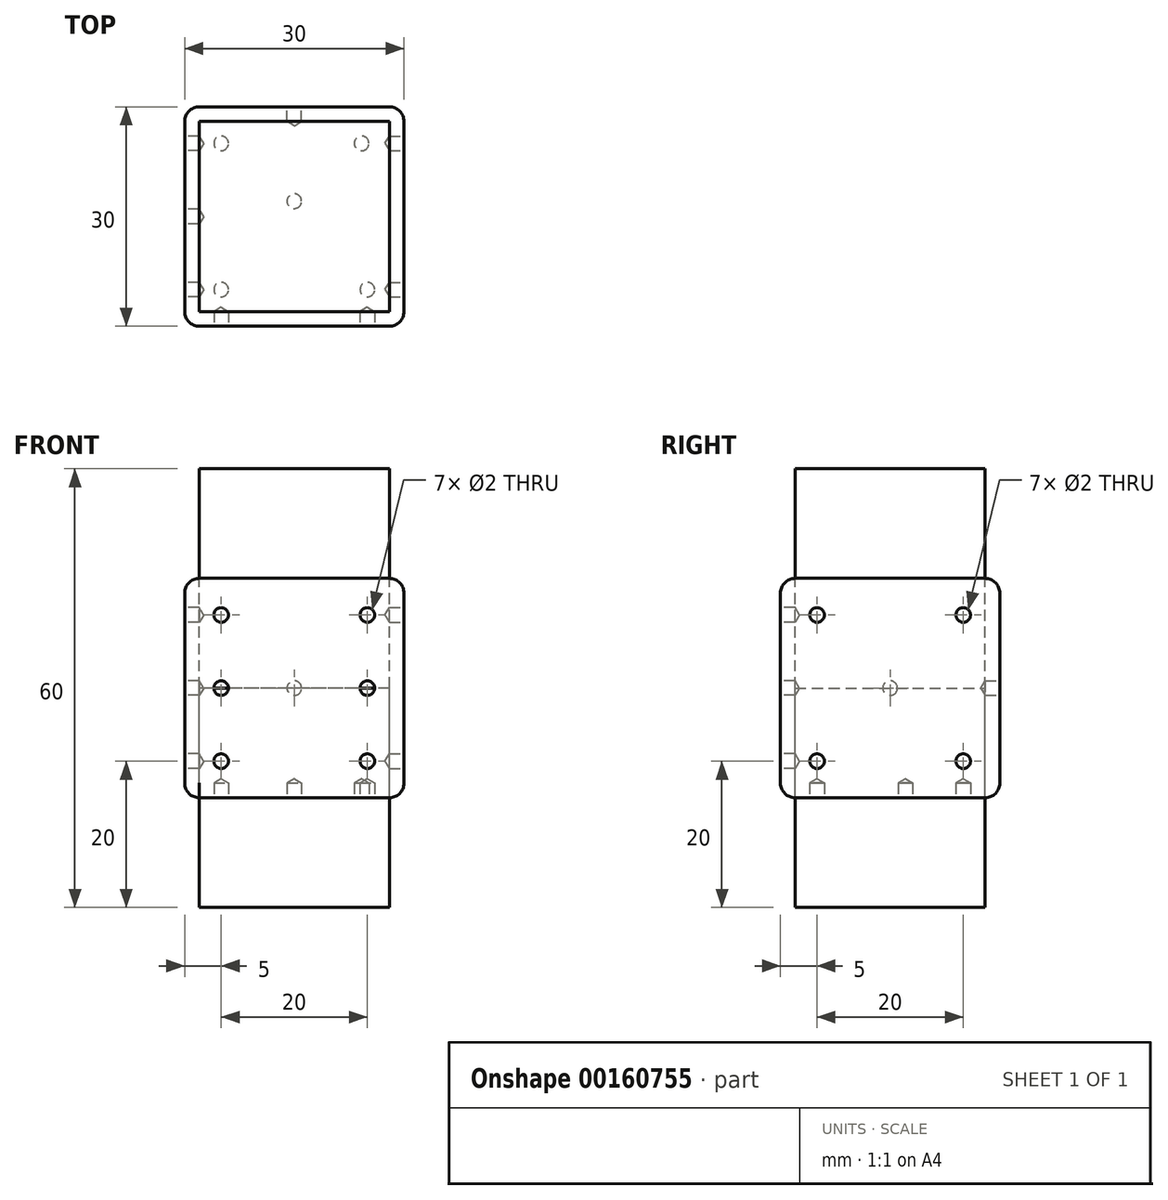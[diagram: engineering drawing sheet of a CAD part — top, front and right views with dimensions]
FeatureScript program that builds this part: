
annotation { "Feature Type Name" : "Feature", "Feature Type Description" : "" }
export const myFeature = defineFeature(function(context is Context, id is Id, definition is map)
    precondition{}
    {
        {
            var Q0;
            Q0=qCreatedBy(makeId("Front.planeOp"),FACE);
            var sketch = newSketch(context, id + "F0", { "sketchPlane" : qUnion([Q0])});
            skLineSegment(sketch, "E0.bottom", {"start": v(15, 15) * mm, "end": v(-15, 15) * mm});
            skLineSegment(sketch, "E0.top", {"start": v(15, -15) * mm, "end": v(-15, -15) * mm});
            skLineSegment(sketch, "E0.left", {"start": v(15, 15) * mm, "end": v(15, -15) * mm});
            skLineSegment(sketch, "E0.right", {"start": v(-15, 15) * mm, "end": v(-15, -15) * mm});
            skPoint(sketch, "E0.middle", {"position": v(0, 0) * mm});
            skLineSegment(sketch, "E1", {"start": v(15, 0) * mm, "end": v(-15, 0) * mm});
            skLineSegment(sketch, "E2", {"start": v(0, 0) * mm, "end": v(0, -15) * mm});
            skLineSegment(sketch, "E3", {"start": v(0, 0) * mm, "end": v(-15, 0) * mm});
            skLineSegment(sketch, "E4", {"start": v(0, 0) * mm, "end": v(0, 15) * mm});
            skPoint(sketch, "E5.middle", {"position": v(-15, 15) * mm});
            skPoint(sketch, "E6.middle", {"position": v(-15, -15) * mm});
            skPoint(sketch, "E7.middle", {"position": v(15, 15) * mm});
            skPoint(sketch, "E8.middle", {"position": v(15, -15) * mm});
            skSolve(sketch);
        }
        {
            var Q0;
            Q0 = qSketchRegion(id + "F0", true);
            extrude(context, id + "F1", {"entities" : qUnion([Q0]), "endBound" : BoundingType.SYMMETRIC, "depth" : 30 * mm});
        }
        {
            var Q0;
            Q0=makeQuery(id+"F1.opExtrude","CAP_EDGE",EDGE,{"disambiguationData":[OSD([sQuery(id+"F0.wireOp",EDGE,"E0.right")])],"isStart":false});
            var Q1;
            Q1=makeQuery(id+"F1.opExtrude","CAP_EDGE",EDGE,{"disambiguationData":[OSD([sQuery(id+"F0.wireOp",EDGE,"E0.top")])],"isStart":false});
            var Q2;
            Q2=makeQuery(id+"F1.opExtrude","SWEPT_EDGE",EDGE,{"disambiguationData":[OSD([sQuery(id+"F0.wireOp",EDGE,"E0.top"),sQuery(id+"F0.wireOp",EDGE,"E0.right")])]});
            var Q3;
            Q3=makeQuery(id+"F1.opExtrude","CAP_EDGE",EDGE,{"disambiguationData":[OSD([sQuery(id+"F0.wireOp",EDGE,"E0.top")])],"isStart":true});
            var Q4;
            Q4=makeQuery(id+"F1.opExtrude","CAP_EDGE",EDGE,{"disambiguationData":[OSD([sQuery(id+"F0.wireOp",EDGE,"E0.right")])],"isStart":true});
            var Q5;
            Q5=makeQuery(id+"F1.opExtrude","SWEPT_EDGE",EDGE,{"disambiguationData":[OSD([sQuery(id+"F0.wireOp",EDGE,"E0.bottom"),sQuery(id+"F0.wireOp",EDGE,"E0.right")])]});
            var Q6;
            Q6=makeQuery(id+"F1.opExtrude","CAP_EDGE",EDGE,{"disambiguationData":[OSD([sQuery(id+"F0.wireOp",EDGE,"E0.bottom")])],"isStart":false});
            var Q7;
            Q7=makeQuery(id+"F1.opExtrude","CAP_FACE",FACE,{"disambiguationData":[OSD([sQuery(id+"F0.wireOp",EDGE,"E0.bottom"),sQuery(id+"F0.wireOp",EDGE,"E0.top"),sQuery(id+"F0.wireOp",EDGE,"E0.left"),sQuery(id+"F0.wireOp",EDGE,"E0.right")])],"isStart":false});
            var Q8;
            Q8=makeQuery(id+"F1.opExtrude","SWEPT_EDGE",EDGE,{"disambiguationData":[OSD([sQuery(id+"F0.wireOp",EDGE,"E0.bottom"),sQuery(id+"F0.wireOp",EDGE,"E0.left")])]});
            var Q9;
            Q9=makeQuery(id+"F1.opExtrude","CAP_EDGE",EDGE,{"disambiguationData":[OSD([sQuery(id+"F0.wireOp",EDGE,"E0.bottom")])],"isStart":true});
            var Q10;
            Q10=makeQuery(id+"F1.opExtrude","CAP_EDGE",EDGE,{"disambiguationData":[OSD([sQuery(id+"F0.wireOp",EDGE,"E0.left")])],"isStart":true});
            var Q11;
            Q11=makeQuery(id+"F1.opExtrude","SWEPT_EDGE",EDGE,{"disambiguationData":[OSD([sQuery(id+"F0.wireOp",EDGE,"E0.top"),sQuery(id+"F0.wireOp",EDGE,"E0.left")])]});
            fillet(context, id + "F2", {"entities" : qUnion([Q0, Q1, Q2, Q3, Q4, Q5, Q6, Q7, Q8, Q9, Q10, Q11]), "radius" : 2 * mm, "tangentPropagation" : true, "allowEdgeOverflow" : false});
        }
        {
            var Q0;
            Q0=makeQuery(id+"F1.opExtrude","CAP_FACE",FACE,{"disambiguationData":[OSD([sQuery(id+"F0.wireOp",EDGE,"E0.bottom"),sQuery(id+"F0.wireOp",EDGE,"E0.top"),sQuery(id+"F0.wireOp",EDGE,"E0.left"),sQuery(id+"F0.wireOp",EDGE,"E0.right")])],"isStart":false});
            var sketch = newSketch(context, id + "F3", { "sketchPlane" : qUnion([Q0])});
            skPoint(sketch, "E9", {"position": v(-10, 10) * mm});
            skPoint(sketch, "E10", {"position": v(10, 10) * mm});
            skPoint(sketch, "E11", {"position": v(-10, 0) * mm});
            skPoint(sketch, "E12", {"position": v(10, 0) * mm});
            skPoint(sketch, "E13", {"position": v(10, -10) * mm});
            skPoint(sketch, "E14", {"position": v(-10, -10) * mm});
            skSolve(sketch);
        }
        {
            var Q0;
            Q0=makeQuery(id+"F1.opExtrude","SWEPT_FACE",FACE,{"disambiguationData":[OSD([sQuery(id+"F0.wireOp",EDGE,"E0.top")])]});
            var sketch = newSketch(context, id + "F4", { "sketchPlane" : qUnion([Q0])});
            skPoint(sketch, "E15", {"position": v(-10, 10) * mm});
            skPoint(sketch, "E16", {"position": v(0, -2.1) * mm});
            skPoint(sketch, "E17", {"position": v(10, 10) * mm});
            skPoint(sketch, "E18", {"position": v(9.21, -10) * mm});
            skPoint(sketch, "E19", {"position": v(-10, -10) * mm});
            skSolve(sketch);
        }
        {
            var Q0;
            Q0=makeQuery(id+"F1.opExtrude","CAP_FACE",FACE,{"disambiguationData":[OSD([sQuery(id+"F0.wireOp",EDGE,"E0.bottom"),sQuery(id+"F0.wireOp",EDGE,"E0.top"),sQuery(id+"F0.wireOp",EDGE,"E0.left"),sQuery(id+"F0.wireOp",EDGE,"E0.right")])],"isStart":true});
            var sketch = newSketch(context, id + "F5", { "sketchPlane" : qUnion([Q0])});
            skPoint(sketch, "E20", {"position": v(0, 0) * mm});
            skSolve(sketch);
        }
        {
            var Q0;
            Q0=makeQuery(id+"F1.opExtrude","SWEPT_FACE",FACE,{"disambiguationData":[OSD([sQuery(id+"F0.wireOp",EDGE,"E0.left")])]});
            var sketch = newSketch(context, id + "F6", { "sketchPlane" : qUnion([Q0])});
            skPoint(sketch, "E21", {"position": v(-10, 10) * mm});
            skPoint(sketch, "E22", {"position": v(-10, -10) * mm});
            skPoint(sketch, "E23", {"position": v(10, -10) * mm});
            skPoint(sketch, "E24", {"position": v(10, 10) * mm});
            skSolve(sketch);
        }
        {
            var Q0;
            Q0=makeQuery(id+"F1.opExtrude","SWEPT_FACE",FACE,{"disambiguationData":[OSD([sQuery(id+"F0.wireOp",EDGE,"E0.right")])]});
            var sketch = newSketch(context, id + "F7", { "sketchPlane" : qUnion([Q0])});
            skPoint(sketch, "E25", {"position": v(0, 0) * mm});
            skPoint(sketch, "E26", {"position": v(10, 10) * mm});
            skPoint(sketch, "E27", {"position": v(-10, -10) * mm});
            skSolve(sketch);
        }
        {
            var Q0;
            Q0=makeQuery(id+"F1.opExtrude","SWEPT_FACE",FACE,{"disambiguationData":[OSD([sQuery(id+"F0.wireOp",EDGE,"E0.top")])]});
            var Q1;
            Q1=makeQuery(id+"F1.opExtrude","SWEPT_FACE",FACE,{"disambiguationData":[OSD([sQuery(id+"F0.wireOp",EDGE,"E0.bottom")])]});
            var Q2;
            {var subQ0=sQuery(id+"F0.wireOp",EDGE,"E0.top");var subQ1=makeQuery(id+"F1.opExtrude","SWEPT_FACE",FACE,{"disambiguationData":[OSD([subQ0])]});Q2=makeQuery(id+"F4.imprint","IMPRINT",FACE,{"disambiguationData":[TD([[makeQuery(id+"F4.imprint","IMPRINT",EDGE,{"derivedFrom":makeQuery(id+"F2.opFillet","BLEND_EDGE",EDGE,{"blendedFrom":[makeQuery(id+"F1.opExtrude","CAP_EDGE",EDGE,{"disambiguationData":[OSD([subQ0])],"isStart":true}),subQ1],"blendedInto":[subQ1]})}),1.0]])]});}
            var Q3;
            Q3 = qSketchRegion(id + "F7", true);
            extrude(context, id + "F8", {"entities" : qUnion([Q0, Q1, Q2, Q3]), "endBound" : BoundingType.SYMMETRIC, "depth" : 30 * mm});
        }
        {
            var Q0;
            Q0=sQuery(id+"F7.wireOp",VERTEX,"E26");
            var Q1;
            Q1=sQuery(id+"F7.wireOp",VERTEX,"E25");
            var Q2;
            Q2=sQuery(id+"F7.wireOp",VERTEX,"E27");
            var Q3;
            Q3=makeQuery(id+"F1.opExtrude","SWEPT_BODY",BODY,{"disambiguationData":[OSD([sQuery(id+"F0.wireOp",EDGE,"E0.bottom"),sQuery(id+"F0.wireOp",EDGE,"E0.top"),sQuery(id+"F0.wireOp",EDGE,"E0.left"),sQuery(id+"F0.wireOp",EDGE,"E0.right")])]});
            hole(context, id + "F9", {"style" : HoleStyle.SIMPLE, "endStyle" : HoleEndStyle.BLIND, "holeDiameter" : 2 * mm, "holeDepth" : 2 * mm, "locations" : qUnion([Q0, Q1, Q2]), "scope" : qUnion([Q3])});
        }
        {
            var Q0;
            Q0=sQuery(id+"F3.wireOp",VERTEX,"E10");
            var Q1;
            Q1=sQuery(id+"F3.wireOp",VERTEX,"E12");
            var Q2;
            Q2=sQuery(id+"F3.wireOp",VERTEX,"E13");
            var Q3;
            Q3=sQuery(id+"F3.wireOp",VERTEX,"E14");
            var Q4;
            Q4=sQuery(id+"F3.wireOp",VERTEX,"E11");
            var Q5;
            Q5=sQuery(id+"F3.wireOp",VERTEX,"E9");
            var Q6;
            Q6=sQuery(id+"F6.wireOp",VERTEX,"E24");
            var Q7;
            Q7=sQuery(id+"F7.wireOp",VERTEX,"E25");
            var Q8;
            Q8=sQuery(id+"F6.wireOp",VERTEX,"E23");
            var Q9;
            Q9=sQuery(id+"F6.wireOp",VERTEX,"E22");
            var Q10;
            Q10=sQuery(id+"F6.wireOp",VERTEX,"E21");
            var Q11;
            Q11=sQuery(id+"F5.wireOp",VERTEX,"E20");
            var Q12;
            Q12=sQuery(id+"F4.wireOp",VERTEX,"E17");
            var Q13;
            Q13=sQuery(id+"F4.wireOp",VERTEX,"E18");
            var Q14;
            Q14=sQuery(id+"F4.wireOp",VERTEX,"E16");
            var Q15;
            Q15=sQuery(id+"F4.wireOp",VERTEX,"E19");
            var Q16;
            Q16=sQuery(id+"F4.wireOp",VERTEX,"E15");
            var Q17;
            Q17=makeQuery(id+"F1.opExtrude","SWEPT_BODY",BODY,{"disambiguationData":[OSD([sQuery(id+"F0.wireOp",EDGE,"E0.bottom"),sQuery(id+"F0.wireOp",EDGE,"E0.top"),sQuery(id+"F0.wireOp",EDGE,"E0.left"),sQuery(id+"F0.wireOp",EDGE,"E0.right")])]});
            hole(context, id + "F10", {"style" : HoleStyle.SIMPLE, "endStyle" : HoleEndStyle.BLIND, "holeDiameter" : 2 * mm, "holeDepth" : 2 * mm, "locations" : qUnion([Q0, Q1, Q2, Q3, Q4, Q5, Q6, Q7, Q8, Q9, Q10, Q11, Q12, Q13, Q14, Q15, Q16]), "scope" : qUnion([Q17])});
        }
    });
